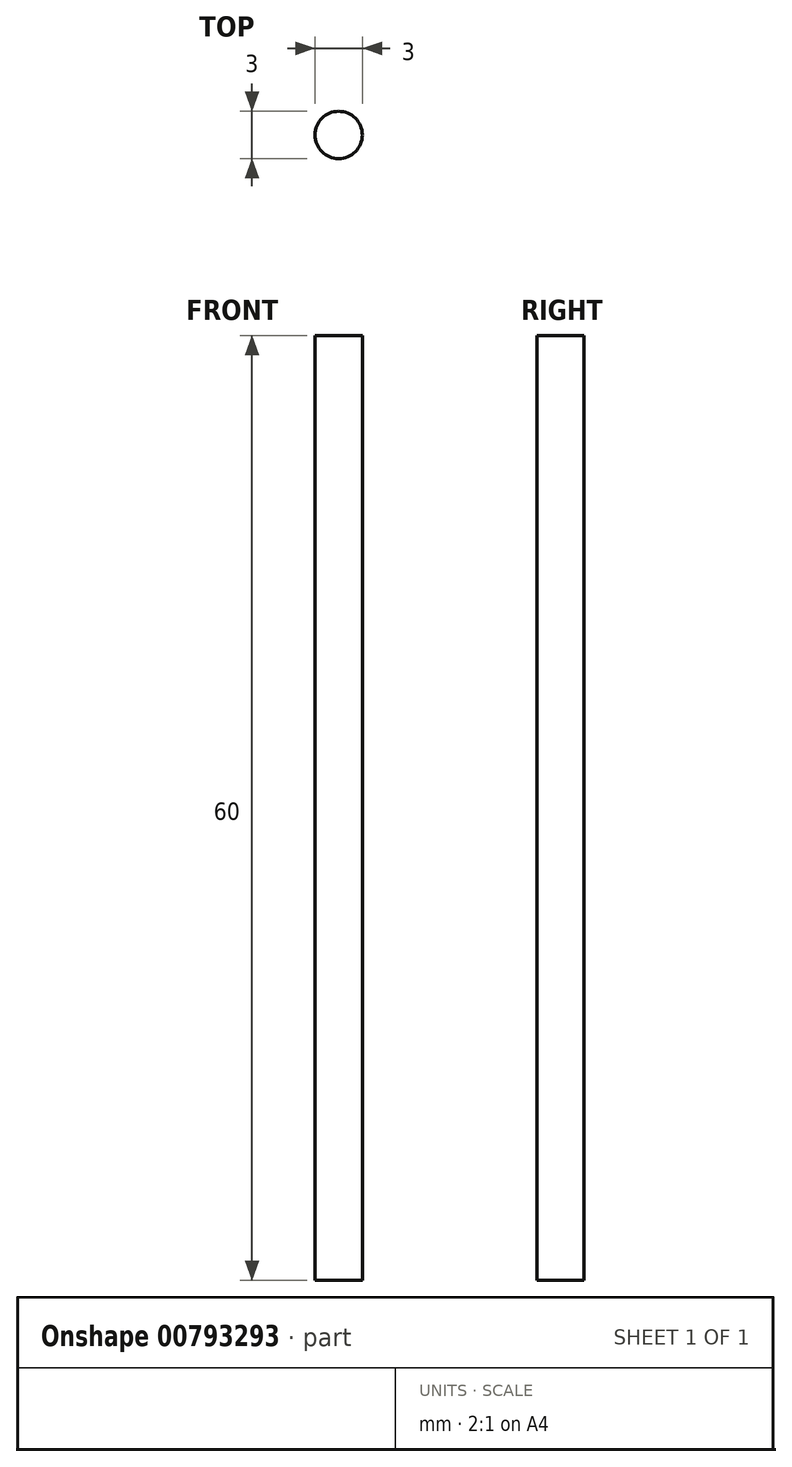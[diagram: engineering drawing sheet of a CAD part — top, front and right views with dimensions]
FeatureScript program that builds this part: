
annotation { "Feature Type Name" : "Feature", "Feature Type Description" : "" }
export const myFeature = defineFeature(function(context is Context, id is Id, definition is map)
    precondition{}
    {
        {
            var Q0;
            Q0=qCreatedBy(makeId("Top.planeOp"),FACE);
            var sketch = newSketch(context, id + "F0", { "sketchPlane" : qUnion([Q0])});
            skCircle(sketch, "E0", {"center": v(0, 0) * mm, "radius": 1.5 * mm});
            skSolve(sketch);
        }
        {
            var Q0;
            Q0 = qSketchRegion(id + "F0", true);
            extrude(context, id + "F1", {"entities" : qUnion([Q0]), "depth" : 60 * mm, "offsetDistance" : 25 * mm});
        }
    });
